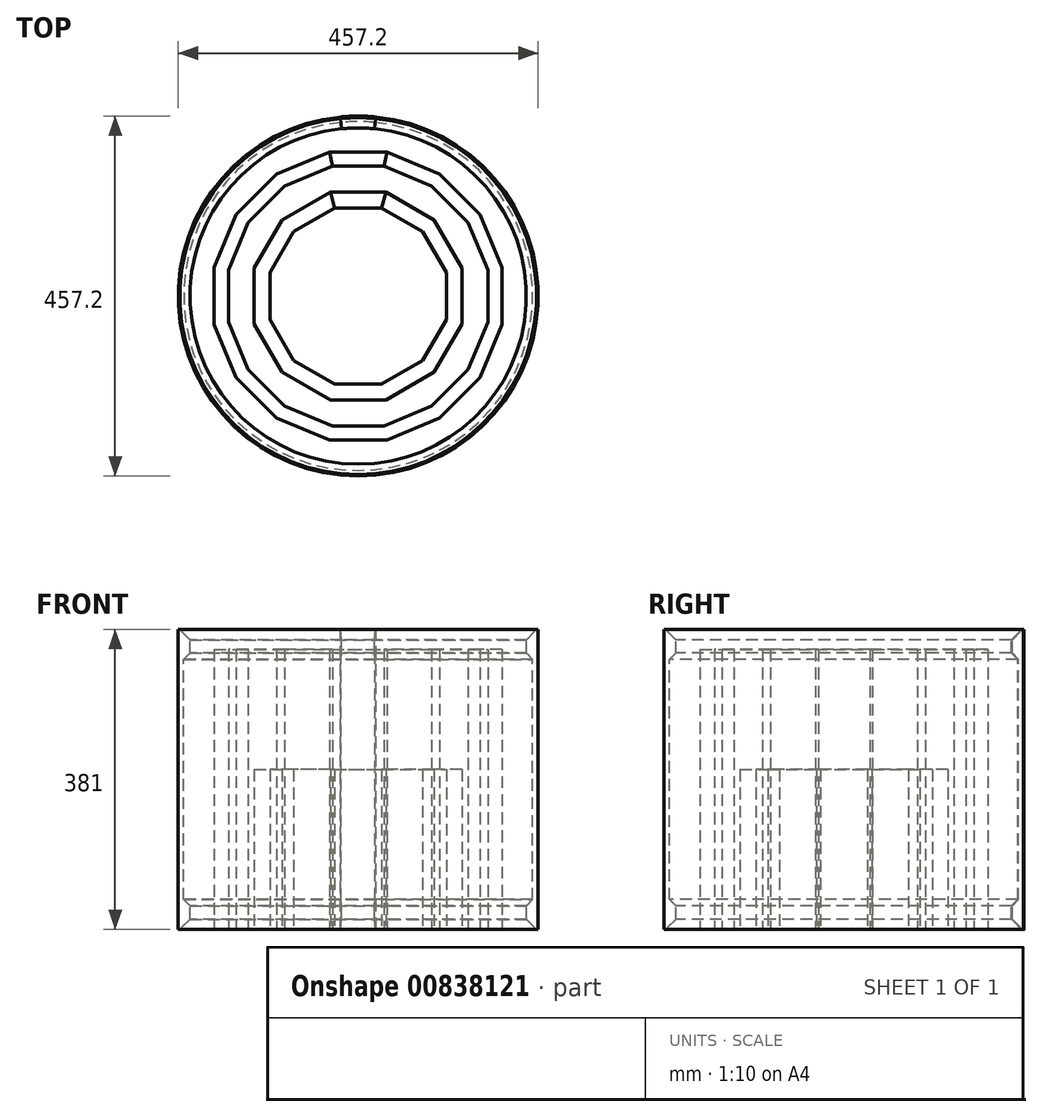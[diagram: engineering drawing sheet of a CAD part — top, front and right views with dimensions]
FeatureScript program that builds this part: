
annotation { "Feature Type Name" : "Feature", "Feature Type Description" : "" }
export const myFeature = defineFeature(function(context is Context, id is Id, definition is map)
    precondition{}
    {
        {
            var Q0;
            Q0=qCreatedBy(makeId("Top.planeOp"),FACE);
            var sketch = newSketch(context, id + "F0", { "sketchPlane" : qUnion([Q0])});
            skCircle(sketch, "E0", {"center": v(0, 0) * mm, "radius": 221.6 * mm, "construction": true});
            skCircle(sketch, "E1", {"center": v(0, 0) * mm, "radius": 228.6 * mm, "construction": true});
            skCircle(sketch, "E2", {"center": v(0, 0) * mm, "radius": 213.6 * mm, "construction": true});
            skCircle(sketch, "E3.cCircle", {"center": v(0, 0) * mm, "radius": 235.6 * mm, "construction": true});
            skLineSegment(sketch, "E3.0", {"start": v(226.55, 68.72) * mm, "end": v(235.6, 23.2) * mm});
            skLineSegment(sketch, "E3.1", {"start": v(235.6, 23.2) * mm, "end": v(235.6, -23.2) * mm});
            skLineSegment(sketch, "E3.2", {"start": v(235.6, -23.2) * mm, "end": v(226.55, -68.72) * mm});
            skLineSegment(sketch, "E3.3", {"start": v(226.55, -68.72) * mm, "end": v(208.79, -111.6) * mm});
            skLineSegment(sketch, "E3.4", {"start": v(208.79, -111.6) * mm, "end": v(183, -150.19) * mm});
            skLineSegment(sketch, "E3.5", {"start": v(183, -150.19) * mm, "end": v(150.19, -183) * mm});
            skLineSegment(sketch, "E3.6", {"start": v(150.19, -183) * mm, "end": v(111.6, -208.79) * mm});
            skLineSegment(sketch, "E3.7", {"start": v(111.6, -208.79) * mm, "end": v(68.72, -226.55) * mm});
            skLineSegment(sketch, "E3.8", {"start": v(68.72, -226.55) * mm, "end": v(23.2, -235.6) * mm});
            skLineSegment(sketch, "E3.9", {"start": v(23.2, -235.6) * mm, "end": v(-23.2, -235.6) * mm});
            skLineSegment(sketch, "E3.10", {"start": v(-23.2, -235.6) * mm, "end": v(-68.72, -226.55) * mm});
            skLineSegment(sketch, "E3.11", {"start": v(-68.72, -226.55) * mm, "end": v(-111.6, -208.79) * mm});
            skLineSegment(sketch, "E3.12", {"start": v(-111.6, -208.79) * mm, "end": v(-150.19, -183) * mm});
            skLineSegment(sketch, "E3.13", {"start": v(-150.19, -183) * mm, "end": v(-183, -150.19) * mm});
            skLineSegment(sketch, "E3.14", {"start": v(-183, -150.19) * mm, "end": v(-208.79, -111.6) * mm});
            skLineSegment(sketch, "E3.15", {"start": v(-208.79, -111.6) * mm, "end": v(-226.55, -68.72) * mm});
            skLineSegment(sketch, "E3.16", {"start": v(-226.55, -68.72) * mm, "end": v(-235.6, -23.2) * mm});
            skLineSegment(sketch, "E3.17", {"start": v(-235.6, -23.2) * mm, "end": v(-235.6, 23.2) * mm});
            skLineSegment(sketch, "E3.18", {"start": v(-235.6, 23.2) * mm, "end": v(-226.55, 68.72) * mm});
            skLineSegment(sketch, "E3.19", {"start": v(-226.55, 68.72) * mm, "end": v(-208.79, 111.6) * mm});
            skLineSegment(sketch, "E3.20", {"start": v(-208.79, 111.6) * mm, "end": v(-183, 150.19) * mm});
            skLineSegment(sketch, "E3.21", {"start": v(-183, 150.19) * mm, "end": v(-150.19, 183) * mm});
            skLineSegment(sketch, "E3.22", {"start": v(-150.19, 183) * mm, "end": v(-111.6, 208.79) * mm});
            skLineSegment(sketch, "E3.23", {"start": v(-111.6, 208.79) * mm, "end": v(-68.72, 226.55) * mm});
            skLineSegment(sketch, "E3.24", {"start": v(-68.72, 226.55) * mm, "end": v(-23.2, 235.6) * mm});
            skLineSegment(sketch, "E3.25", {"start": v(-23.2, 235.6) * mm, "end": v(23.2, 235.6) * mm});
            skLineSegment(sketch, "E3.26", {"start": v(23.2, 235.6) * mm, "end": v(68.72, 226.55) * mm});
            skLineSegment(sketch, "E3.27", {"start": v(68.72, 226.55) * mm, "end": v(111.6, 208.79) * mm});
            skLineSegment(sketch, "E3.28", {"start": v(111.6, 208.79) * mm, "end": v(150.19, 183) * mm});
            skLineSegment(sketch, "E3.29", {"start": v(150.19, 183) * mm, "end": v(183, 150.19) * mm});
            skLineSegment(sketch, "E3.30", {"start": v(183, 150.19) * mm, "end": v(208.79, 111.6) * mm});
            skLineSegment(sketch, "E3.31", {"start": v(208.79, 111.6) * mm, "end": v(226.55, 68.72) * mm});
            skPoint(sketch, "E3.0.midPoint", {"position": v(231.07, 45.96) * mm});
            skLineSegment(sketch, "E4.0", {"start": v(-161.25, 132.34) * mm, "end": v(-132.34, 161.25) * mm});
            skLineSegment(sketch, "E4.1", {"start": v(-183.97, 98.34) * mm, "end": v(-161.25, 132.34) * mm});
            skLineSegment(sketch, "E4.2", {"start": v(-199.62, 60.55) * mm, "end": v(-183.97, 98.34) * mm});
            skLineSegment(sketch, "E4.3", {"start": v(-207.6, 20.45) * mm, "end": v(-199.62, 60.55) * mm});
            skLineSegment(sketch, "E4.4", {"start": v(-207.6, -20.45) * mm, "end": v(-207.6, 20.45) * mm});
            skLineSegment(sketch, "E4.5", {"start": v(-199.62, -60.55) * mm, "end": v(-207.6, -20.45) * mm});
            skLineSegment(sketch, "E4.6", {"start": v(-183.97, -98.34) * mm, "end": v(-199.62, -60.55) * mm});
            skLineSegment(sketch, "E4.7", {"start": v(-161.25, -132.34) * mm, "end": v(-183.97, -98.34) * mm});
            skLineSegment(sketch, "E4.8", {"start": v(-132.34, -161.25) * mm, "end": v(-161.25, -132.34) * mm});
            skLineSegment(sketch, "E4.9", {"start": v(199.62, 60.55) * mm, "end": v(207.6, 20.45) * mm});
            skLineSegment(sketch, "E4.10", {"start": v(183.97, 98.34) * mm, "end": v(199.62, 60.55) * mm});
            skLineSegment(sketch, "E4.11", {"start": v(161.25, 132.34) * mm, "end": v(183.97, 98.34) * mm});
            skLineSegment(sketch, "E4.12", {"start": v(132.34, 161.25) * mm, "end": v(161.25, 132.34) * mm});
            skLineSegment(sketch, "E4.13", {"start": v(98.34, 183.97) * mm, "end": v(132.34, 161.25) * mm});
            skLineSegment(sketch, "E4.14", {"start": v(60.55, 199.62) * mm, "end": v(98.34, 183.97) * mm});
            skLineSegment(sketch, "E4.15", {"start": v(-98.34, 183.97) * mm, "end": v(-60.55, 199.62) * mm});
            skLineSegment(sketch, "E4.16", {"start": v(-60.55, 199.62) * mm, "end": v(-20.45, 207.6) * mm});
            skLineSegment(sketch, "E4.17", {"start": v(-20.45, 207.6) * mm, "end": v(20.45, 207.6) * mm});
            skLineSegment(sketch, "E4.18", {"start": v(20.45, 207.6) * mm, "end": v(60.55, 199.62) * mm});
            skLineSegment(sketch, "E4.19", {"start": v(207.6, 20.45) * mm, "end": v(207.6, -20.45) * mm});
            skLineSegment(sketch, "E4.20", {"start": v(207.6, -20.45) * mm, "end": v(199.62, -60.55) * mm});
            skLineSegment(sketch, "E4.21", {"start": v(199.62, -60.55) * mm, "end": v(183.97, -98.34) * mm});
            skLineSegment(sketch, "E4.22", {"start": v(183.97, -98.34) * mm, "end": v(161.25, -132.34) * mm});
            skLineSegment(sketch, "E4.23", {"start": v(161.25, -132.34) * mm, "end": v(132.34, -161.25) * mm});
            skLineSegment(sketch, "E4.24", {"start": v(132.34, -161.25) * mm, "end": v(98.34, -183.97) * mm});
            skLineSegment(sketch, "E4.25", {"start": v(98.34, -183.97) * mm, "end": v(60.55, -199.62) * mm});
            skLineSegment(sketch, "E4.26", {"start": v(60.55, -199.62) * mm, "end": v(20.45, -207.6) * mm});
            skLineSegment(sketch, "E4.27", {"start": v(20.45, -207.6) * mm, "end": v(-20.45, -207.6) * mm});
            skLineSegment(sketch, "E4.28", {"start": v(-132.34, 161.25) * mm, "end": v(-98.34, 183.97) * mm});
            skLineSegment(sketch, "E4.29", {"start": v(-20.45, -207.6) * mm, "end": v(-60.55, -199.62) * mm});
            skLineSegment(sketch, "E4.30", {"start": v(-60.55, -199.62) * mm, "end": v(-98.34, -183.97) * mm});
            skLineSegment(sketch, "E4.31", {"start": v(-98.34, -183.97) * mm, "end": v(-132.34, -161.25) * mm});
            skLineSegment(sketch, "E5", {"start": v(-23.2, 235.6) * mm, "end": v(-20.45, 207.6) * mm});
            skLineSegment(sketch, "E6", {"start": v(23.2, 235.6) * mm, "end": v(20.45, 207.6) * mm});
            skSolve(sketch);
        }
        {
            var Q0;
            Q0=makeQuery(id+"F0.imprint","IMPRINT",FACE,{"disambiguationData":[TD([[makeQuery(id+"F0.imprint","IMPRINT",EDGE,{"derivedFrom":sQuery(id+"F0.wireOp",EDGE,"E3.25")}),-1.0]])]});
            extrude(context, id + "F1", {"entities" : qUnion([Q0]), "depth" : 381 * mm, "offsetDistance" : 25 * mm});
        }
        {
            var Q0;
            Q0=makeQuery(id+"F0.imprint","IMPRINT",FACE,{"disambiguationData":[TD([[makeQuery(id+"F0.imprint","IMPRINT",EDGE,{"derivedFrom":sQuery(id+"F0.wireOp",EDGE,"E3.0")}),-1.0]])]});
            var Q1;
            Q1=makeQuery(id+"F1.opExtrude","CAP_FACE",FACE,{"disambiguationData":[OSD([sQuery(id+"F0.wireOp",EDGE,"E3.25"),sQuery(id+"F0.wireOp",EDGE,"E4.17"),sQuery(id+"F0.wireOp",EDGE,"E5"),sQuery(id+"F0.wireOp",EDGE,"E6")])],"isStart":false});
            extrude(context, id + "F2", {"entities" : qUnion([Q0]), "endBound" : BoundingType.UP_TO_SURFACE, "depth" : 25 * mm, "endBoundEntityFace" : qUnion([Q1]), "offsetDistance" : 25 * mm});
        }
        {
            var Q0;
            Q0=qCreatedBy(makeId("Front.planeOp"),FACE);
            var sketch = newSketch(context, id + "F3", { "sketchPlane" : qUnion([Q0])});
            skLineSegment(sketch, "E7", {"start": v(-228.6, 393.4) * mm, "end": v(-228.6, -35.86) * mm});
            skLineSegment(sketch, "E8", {"start": v(-213.6, -35.86) * mm, "end": v(-213.6, 30) * mm});
            skLineSegment(sketch, "E9", {"start": v(-213.6, 30) * mm, "end": v(-221.6, 38) * mm});
            skLineSegment(sketch, "E10", {"start": v(-221.6, 38) * mm, "end": v(-221.6, 343) * mm});
            skLineSegment(sketch, "E11", {"start": v(-221.6, 343) * mm, "end": v(-213.6, 351) * mm});
            skLineSegment(sketch, "E12", {"start": v(-213.6, 351) * mm, "end": v(-213.6, 393.4) * mm});
            skLineSegment(sketch, "E13", {"start": v(0, 0) * mm, "end": v(0, 397.13) * mm, "construction": true});
            skLineSegment(sketch, "E14.bottom", {"start": v(-342.05, 393.4) * mm, "end": v(-228.6, 393.4) * mm});
            skLineSegment(sketch, "E14.top", {"start": v(-342.05, -35.86) * mm, "end": v(-228.6, -35.86) * mm});
            skLineSegment(sketch, "E14.left", {"start": v(-342.05, 393.4) * mm, "end": v(-342.05, -35.86) * mm});
            skLineSegment(sketch, "E14.right", {"start": v(-190.52, 393.4) * mm, "end": v(-190.52, -35.86) * mm});
            skLineSegment(sketch, "E15.trimOffspring", {"start": v(-213.6, 393.4) * mm, "end": v(-190.52, 393.4) * mm});
            skPoint(sketch, "E16.orphan", {"position": v(-228.6, 397.13) * mm});
            skPoint(sketch, "E17.orphan", {"position": v(-213.6, 397.13) * mm});
            skLineSegment(sketch, "E18.trimOffspring", {"start": v(-213.6, -35.86) * mm, "end": v(-190.52, -35.86) * mm});
            skSolve(sketch);
        }
        {
            var Q0;
            Q0 = qSketchRegion(id + "F3", true);
            var Q1;
            Q1=sQuery(id+"F3.wireOp",EDGE,"E13");
            revolve(context, id + "F4", {"operationType" : NewBodyOperationType.REMOVE, "surfaceOperationType" : NewSurfaceOperationType.NEW, "entities" : qUnion([Q0]), "axis" : qUnion([Q1]), "revolveType" : RevolveType.FULL, "oppositeDirection" : true});
        }
        {
            var Q0;
            Q0=makeQuery(id+"F4.boolean.opBoolean","INTERSECT",EDGE,{"derivedFrom":[makeQuery(id+"F2.opExtrude","CAP_FACE",FACE,{"disambiguationData":[OSD([sQuery(id+"F0.wireOp",EDGE,"E3.25"),sQuery(id+"F0.wireOp",EDGE,"E4.17"),sQuery(id+"F0.wireOp",EDGE,"E5"),sQuery(id+"F0.wireOp",EDGE,"E6")])],"isStart":false}),makeQuery(id+"F4.opRevolve","SWEPT_FACE",FACE,{"disambiguationData":[OSD([sQuery(id+"F3.wireOp",EDGE,"E12")])]})]});
            var Q1;
            Q1=makeQuery(id+"F4.boolean.opBoolean","INTERSECT",EDGE,{"derivedFrom":[makeQuery(id+"F1.opExtrude","CAP_FACE",FACE,{"disambiguationData":[OSD([sQuery(id+"F0.wireOp",EDGE,"E3.25"),sQuery(id+"F0.wireOp",EDGE,"E4.17"),sQuery(id+"F0.wireOp",EDGE,"E5"),sQuery(id+"F0.wireOp",EDGE,"E6")])],"isStart":false}),makeQuery(id+"F4.opRevolve","SWEPT_FACE",FACE,{"disambiguationData":[OSD([sQuery(id+"F3.wireOp",EDGE,"E12")])]})]});
            var Q2;
            Q2=makeQuery(id+"F4.boolean.opBoolean","INTERSECT",EDGE,{"derivedFrom":[makeQuery(id+"F1.opExtrude","CAP_FACE",FACE,{"disambiguationData":[OSD([sQuery(id+"F0.wireOp",EDGE,"E3.25"),sQuery(id+"F0.wireOp",EDGE,"E4.17"),sQuery(id+"F0.wireOp",EDGE,"E5"),sQuery(id+"F0.wireOp",EDGE,"E6")])],"isStart":true}),makeQuery(id+"F4.opRevolve","SWEPT_FACE",FACE,{"disambiguationData":[OSD([sQuery(id+"F3.wireOp",EDGE,"E8")])]})]});
            var Q3;
            Q3=makeQuery(id+"F4.boolean.opBoolean","INTERSECT",EDGE,{"derivedFrom":[makeQuery(id+"F2.opExtrude","CAP_FACE",FACE,{"disambiguationData":[OSD([sQuery(id+"F0.wireOp",EDGE,"E3.0"),sQuery(id+"F0.wireOp",EDGE,"E3.1"),sQuery(id+"F0.wireOp",EDGE,"E3.2"),sQuery(id+"F0.wireOp",EDGE,"E3.3"),sQuery(id+"F0.wireOp",EDGE,"E3.4"),sQuery(id+"F0.wireOp",EDGE,"E3.5"),sQuery(id+"F0.wireOp",EDGE,"E3.6"),sQuery(id+"F0.wireOp",EDGE,"E3.7"),sQuery(id+"F0.wireOp",EDGE,"E3.8"),sQuery(id+"F0.wireOp",EDGE,"E3.9"),sQuery(id+"F0.wireOp",EDGE,"E3.10"),sQuery(id+"F0.wireOp",EDGE,"E3.11"),sQuery(id+"F0.wireOp",EDGE,"E3.12"),sQuery(id+"F0.wireOp",EDGE,"E3.13"),sQuery(id+"F0.wireOp",EDGE,"E3.14"),sQuery(id+"F0.wireOp",EDGE,"E3.15"),sQuery(id+"F0.wireOp",EDGE,"E3.16"),sQuery(id+"F0.wireOp",EDGE,"E3.17"),sQuery(id+"F0.wireOp",EDGE,"E3.18"),sQuery(id+"F0.wireOp",EDGE,"E3.19"),sQuery(id+"F0.wireOp",EDGE,"E3.20"),sQuery(id+"F0.wireOp",EDGE,"E3.21"),sQuery(id+"F0.wireOp",EDGE,"E3.22"),sQuery(id+"F0.wireOp",EDGE,"E3.23"),sQuery(id+"F0.wireOp",EDGE,"E3.24"),sQuery(id+"F0.wireOp",EDGE,"E3.26"),sQuery(id+"F0.wireOp",EDGE,"E3.27"),sQuery(id+"F0.wireOp",EDGE,"E3.28"),sQuery(id+"F0.wireOp",EDGE,"E3.29"),sQuery(id+"F0.wireOp",EDGE,"E3.30"),sQuery(id+"F0.wireOp",EDGE,"E3.31"),sQuery(id+"F0.wireOp",EDGE,"E4.0"),sQuery(id+"F0.wireOp",EDGE,"E4.1"),sQuery(id+"F0.wireOp",EDGE,"E4.2"),sQuery(id+"F0.wireOp",EDGE,"E4.3"),sQuery(id+"F0.wireOp",EDGE,"E4.4"),sQuery(id+"F0.wireOp",EDGE,"E4.5"),sQuery(id+"F0.wireOp",EDGE,"E4.6"),sQuery(id+"F0.wireOp",EDGE,"E4.7"),sQuery(id+"F0.wireOp",EDGE,"E4.8"),sQuery(id+"F0.wireOp",EDGE,"E4.9"),sQuery(id+"F0.wireOp",EDGE,"E4.10"),sQuery(id+"F0.wireOp",EDGE,"E4.11"),sQuery(id+"F0.wireOp",EDGE,"E4.12"),sQuery(id+"F0.wireOp",EDGE,"E4.13"),sQuery(id+"F0.wireOp",EDGE,"E4.14"),sQuery(id+"F0.wireOp",EDGE,"E4.15"),sQuery(id+"F0.wireOp",EDGE,"E4.16"),sQuery(id+"F0.wireOp",EDGE,"E4.18"),sQuery(id+"F0.wireOp",EDGE,"E4.19"),sQuery(id+"F0.wireOp",EDGE,"E4.20"),sQuery(id+"F0.wireOp",EDGE,"E4.21"),sQuery(id+"F0.wireOp",EDGE,"E4.22"),sQuery(id+"F0.wireOp",EDGE,"E4.23"),sQuery(id+"F0.wireOp",EDGE,"E4.24"),sQuery(id+"F0.wireOp",EDGE,"E4.25"),sQuery(id+"F0.wireOp",EDGE,"E4.26"),sQuery(id+"F0.wireOp",EDGE,"E4.27"),sQuery(id+"F0.wireOp",EDGE,"E4.28"),sQuery(id+"F0.wireOp",EDGE,"E4.29"),sQuery(id+"F0.wireOp",EDGE,"E4.30"),sQuery(id+"F0.wireOp",EDGE,"E4.31"),sQuery(id+"F0.wireOp",EDGE,"E5"),sQuery(id+"F0.wireOp",EDGE,"E6")])],"isStart":true}),makeQuery(id+"F4.opRevolve","SWEPT_FACE",FACE,{"disambiguationData":[OSD([sQuery(id+"F3.wireOp",EDGE,"E8")])]})]});
            chamfer(context, id + "F5", {"entities" : qUnion([Q0, Q1, Q2, Q3]), "width" : 13 * mm, "tangentPropagation" : true});
        }
        {
            var Q0;
            Q0=qCreatedBy(makeId("Top.planeOp"),FACE);
            var sketch = newSketch(context, id + "F6", { "sketchPlane" : qUnion([Q0])});
            skCircle(sketch, "E19", {"center": v(0, 0) * mm, "radius": 170.8 * mm, "construction": true});
            skCircle(sketch, "E20", {"center": v(0, 0) * mm, "radius": 177.8 * mm, "construction": true});
            skCircle(sketch, "E21.cCircle", {"center": v(0, 0) * mm, "radius": 182.8 * mm, "construction": true});
            skLineSegment(sketch, "E21.0", {"start": v(154.97, 103.55) * mm, "end": v(182.8, 36.36) * mm});
            skLineSegment(sketch, "E21.1", {"start": v(182.8, 36.36) * mm, "end": v(182.8, -36.36) * mm});
            skLineSegment(sketch, "E21.2", {"start": v(182.8, -36.36) * mm, "end": v(154.97, -103.55) * mm});
            skLineSegment(sketch, "E21.3", {"start": v(154.97, -103.55) * mm, "end": v(103.55, -154.97) * mm});
            skLineSegment(sketch, "E21.4", {"start": v(103.55, -154.97) * mm, "end": v(36.36, -182.8) * mm});
            skLineSegment(sketch, "E21.5", {"start": v(36.36, -182.8) * mm, "end": v(-36.36, -182.8) * mm});
            skLineSegment(sketch, "E21.6", {"start": v(-36.36, -182.8) * mm, "end": v(-103.55, -154.97) * mm});
            skLineSegment(sketch, "E21.7", {"start": v(-103.55, -154.97) * mm, "end": v(-154.97, -103.55) * mm});
            skLineSegment(sketch, "E21.8", {"start": v(-154.97, -103.55) * mm, "end": v(-182.8, -36.36) * mm});
            skLineSegment(sketch, "E21.9", {"start": v(-182.8, -36.36) * mm, "end": v(-182.8, 36.36) * mm});
            skLineSegment(sketch, "E21.10", {"start": v(-182.8, 36.36) * mm, "end": v(-154.97, 103.55) * mm});
            skLineSegment(sketch, "E21.11", {"start": v(-154.97, 103.55) * mm, "end": v(-103.55, 154.97) * mm});
            skLineSegment(sketch, "E21.12", {"start": v(-103.55, 154.97) * mm, "end": v(-36.36, 182.8) * mm});
            skLineSegment(sketch, "E21.13", {"start": v(-36.36, 182.8) * mm, "end": v(36.36, 182.8) * mm});
            skLineSegment(sketch, "E21.14", {"start": v(36.36, 182.8) * mm, "end": v(103.55, 154.97) * mm});
            skLineSegment(sketch, "E21.15", {"start": v(103.55, 154.97) * mm, "end": v(154.97, 103.55) * mm});
            skPoint(sketch, "E21.0.midPoint", {"position": v(168.89, 69.95) * mm});
            skLineSegment(sketch, "E22.0", {"start": v(93.35, 139.71) * mm, "end": v(139.71, 93.35) * mm});
            skLineSegment(sketch, "E22.1", {"start": v(32.78, 164.8) * mm, "end": v(93.35, 139.71) * mm});
            skLineSegment(sketch, "E22.2", {"start": v(-32.78, 164.8) * mm, "end": v(32.78, 164.8) * mm});
            skLineSegment(sketch, "E22.3", {"start": v(-93.35, 139.71) * mm, "end": v(-32.78, 164.8) * mm});
            skLineSegment(sketch, "E22.4", {"start": v(-139.71, 93.35) * mm, "end": v(-93.35, 139.71) * mm});
            skLineSegment(sketch, "E22.5", {"start": v(93.35, -139.71) * mm, "end": v(32.78, -164.8) * mm});
            skLineSegment(sketch, "E22.6", {"start": v(139.71, -93.35) * mm, "end": v(93.35, -139.71) * mm});
            skLineSegment(sketch, "E22.7", {"start": v(164.8, -32.78) * mm, "end": v(139.71, -93.35) * mm});
            skLineSegment(sketch, "E22.8", {"start": v(164.8, 32.78) * mm, "end": v(164.8, -32.78) * mm});
            skLineSegment(sketch, "E22.9", {"start": v(32.78, -164.8) * mm, "end": v(-32.78, -164.8) * mm});
            skLineSegment(sketch, "E22.10", {"start": v(-32.78, -164.8) * mm, "end": v(-93.35, -139.71) * mm});
            skLineSegment(sketch, "E22.11", {"start": v(-93.35, -139.71) * mm, "end": v(-139.71, -93.35) * mm});
            skLineSegment(sketch, "E22.12", {"start": v(-139.71, -93.35) * mm, "end": v(-164.8, -32.78) * mm});
            skLineSegment(sketch, "E22.13", {"start": v(-164.8, -32.78) * mm, "end": v(-164.8, 32.78) * mm});
            skLineSegment(sketch, "E22.14", {"start": v(139.71, 93.35) * mm, "end": v(164.8, 32.78) * mm});
            skLineSegment(sketch, "E22.15", {"start": v(-164.8, 32.78) * mm, "end": v(-139.71, 93.35) * mm});
            skLineSegment(sketch, "E23", {"start": v(-36.36, 182.8) * mm, "end": v(-32.78, 164.8) * mm});
            skLineSegment(sketch, "E24", {"start": v(36.36, 182.8) * mm, "end": v(32.78, 164.8) * mm});
            skSolve(sketch);
        }
        {
            var Q0;
            Q0=makeQuery(id+"F6.imprint","IMPRINT",FACE,{"disambiguationData":[TD([[makeQuery(id+"F6.imprint","IMPRINT",EDGE,{"derivedFrom":sQuery(id+"F6.wireOp",EDGE,"E21.13")}),-1.0]])]});
            extrude(context, id + "F7", {"entities" : qUnion([Q0]), "depth" : 355.6 * mm, "offsetDistance" : 25 * mm});
        }
        {
            var Q0;
            Q0=makeQuery(id+"F6.imprint","IMPRINT",FACE,{"disambiguationData":[TD([[makeQuery(id+"F6.imprint","IMPRINT",EDGE,{"derivedFrom":sQuery(id+"F6.wireOp",EDGE,"E21.0")}),-1.0]])]});
            var Q1;
            Q1=makeQuery(id+"F7.opExtrude","CAP_FACE",FACE,{"disambiguationData":[OSD([sQuery(id+"F6.wireOp",EDGE,"E21.13"),sQuery(id+"F6.wireOp",EDGE,"E22.2"),sQuery(id+"F6.wireOp",EDGE,"E23"),sQuery(id+"F6.wireOp",EDGE,"E24")])],"isStart":false});
            extrude(context, id + "F8", {"entities" : qUnion([Q0]), "endBound" : BoundingType.UP_TO_SURFACE, "depth" : 25 * mm, "endBoundEntityFace" : qUnion([Q1]), "offsetDistance" : 25 * mm});
        }
        {
            var Q0;
            Q0=qCreatedBy(makeId("Top.planeOp"),FACE);
            var sketch = newSketch(context, id + "F9", { "sketchPlane" : qUnion([Q0])});
            skCircle(sketch, "E25", {"center": v(0, 0) * mm, "radius": 120 * mm, "construction": true});
            skCircle(sketch, "E26", {"center": v(0, 0) * mm, "radius": 127 * mm, "construction": true});
            skCircle(sketch, "E27.cCircle", {"center": v(0, 0) * mm, "radius": 132 * mm, "construction": true});
            skLineSegment(sketch, "E27.0", {"start": v(132, 35.37) * mm, "end": v(132, -35.37) * mm});
            skLineSegment(sketch, "E27.1", {"start": v(132, -35.37) * mm, "end": v(96.63, -96.63) * mm});
            skLineSegment(sketch, "E27.2", {"start": v(96.63, -96.63) * mm, "end": v(35.37, -132) * mm});
            skLineSegment(sketch, "E27.3", {"start": v(35.37, -132) * mm, "end": v(-35.37, -132) * mm});
            skLineSegment(sketch, "E27.4", {"start": v(-35.37, -132) * mm, "end": v(-96.63, -96.63) * mm});
            skLineSegment(sketch, "E27.5", {"start": v(-96.63, -96.63) * mm, "end": v(-132, -35.37) * mm});
            skLineSegment(sketch, "E27.6", {"start": v(-132, -35.37) * mm, "end": v(-132, 35.37) * mm});
            skLineSegment(sketch, "E27.7", {"start": v(-132, 35.37) * mm, "end": v(-96.63, 96.63) * mm});
            skLineSegment(sketch, "E27.8", {"start": v(-96.63, 96.63) * mm, "end": v(-35.37, 132) * mm});
            skLineSegment(sketch, "E27.9", {"start": v(-35.37, 132) * mm, "end": v(35.37, 132) * mm});
            skLineSegment(sketch, "E27.10", {"start": v(35.37, 132) * mm, "end": v(96.63, 96.63) * mm});
            skLineSegment(sketch, "E27.11", {"start": v(96.63, 96.63) * mm, "end": v(132, 35.37) * mm});
            skPoint(sketch, "E27.0.midPoint", {"position": v(132, 0) * mm});
            skLineSegment(sketch, "E28.0", {"start": v(30.01, -112) * mm, "end": v(-30.01, -112) * mm});
            skLineSegment(sketch, "E28.1", {"start": v(-81.99, 81.99) * mm, "end": v(-30.01, 112) * mm});
            skLineSegment(sketch, "E28.2", {"start": v(-112, 30.01) * mm, "end": v(-81.99, 81.99) * mm});
            skLineSegment(sketch, "E28.3", {"start": v(-112, -30.01) * mm, "end": v(-112, 30.01) * mm});
            skLineSegment(sketch, "E28.4", {"start": v(-81.99, -81.99) * mm, "end": v(-112, -30.01) * mm});
            skLineSegment(sketch, "E28.5", {"start": v(-30.01, 112) * mm, "end": v(30.01, 112) * mm});
            skLineSegment(sketch, "E28.6", {"start": v(-30.01, -112) * mm, "end": v(-81.99, -81.99) * mm});
            skLineSegment(sketch, "E28.7", {"start": v(30.01, 112) * mm, "end": v(81.99, 81.99) * mm});
            skLineSegment(sketch, "E28.8", {"start": v(81.99, 81.99) * mm, "end": v(112, 30.01) * mm});
            skLineSegment(sketch, "E28.9", {"start": v(112, 30.01) * mm, "end": v(112, -30.01) * mm});
            skLineSegment(sketch, "E28.10", {"start": v(112, -30.01) * mm, "end": v(81.99, -81.99) * mm});
            skLineSegment(sketch, "E28.11", {"start": v(81.99, -81.99) * mm, "end": v(30.01, -112) * mm});
            skLineSegment(sketch, "E29", {"start": v(-35.37, 132) * mm, "end": v(-30.01, 112) * mm});
            skLineSegment(sketch, "E30", {"start": v(35.37, 132) * mm, "end": v(30.01, 112) * mm});
            skSolve(sketch);
        }
        {
            var Q0;
            Q0=makeQuery(id+"F9.imprint","IMPRINT",FACE,{"disambiguationData":[TD([[makeQuery(id+"F9.imprint","IMPRINT",EDGE,{"derivedFrom":sQuery(id+"F9.wireOp",EDGE,"E27.9")}),-1.0]])]});
            extrude(context, id + "F10", {"entities" : qUnion([Q0]), "depth" : 203.2 * mm, "offsetDistance" : 25 * mm});
        }
        {
            var Q0;
            Q0=makeQuery(id+"F9.imprint","IMPRINT",FACE,{"disambiguationData":[TD([[makeQuery(id+"F9.imprint","IMPRINT",EDGE,{"derivedFrom":sQuery(id+"F9.wireOp",EDGE,"E27.0")}),-1.0]])]});
            var Q1;
            Q1=makeQuery(id+"F10.opExtrude","CAP_FACE",FACE,{"disambiguationData":[OSD([sQuery(id+"F9.wireOp",EDGE,"E27.9"),sQuery(id+"F9.wireOp",EDGE,"E28.5"),sQuery(id+"F9.wireOp",EDGE,"E29"),sQuery(id+"F9.wireOp",EDGE,"E30")])],"isStart":false});
            extrude(context, id + "F11", {"entities" : qUnion([Q0]), "endBound" : BoundingType.UP_TO_SURFACE, "depth" : 25 * mm, "endBoundEntityFace" : qUnion([Q1]), "offsetDistance" : 25 * mm});
        }
    });
